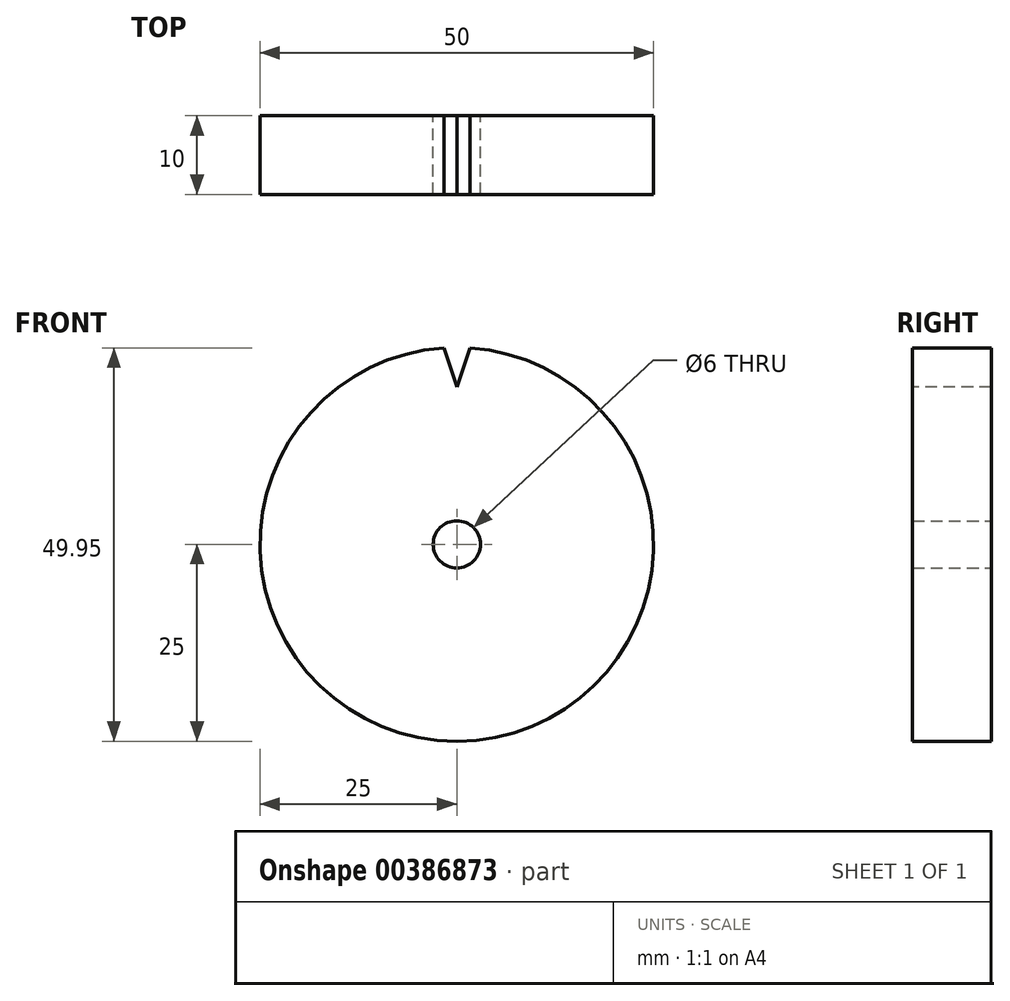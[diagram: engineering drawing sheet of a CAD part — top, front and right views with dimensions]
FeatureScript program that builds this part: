
annotation { "Feature Type Name" : "Feature", "Feature Type Description" : "" }
export const myFeature = defineFeature(function(context is Context, id is Id, definition is map)
    precondition{}
    {
        {
            var Q0;
            Q0=qCreatedBy(makeId("Front.planeOp"),FACE);
            var sketch = newSketch(context, id + "F0", { "sketchPlane" : qUnion([Q0])});
            skCircle(sketch, "E0", {"center": v(0, 0) * mm, "radius": 25 * mm});
            skCircle(sketch, "E1", {"center": v(0, 0) * mm, "radius": 3 * mm});
            skSolve(sketch);
        }
        {
            var Q0;
            Q0 = qSketchRegion(id + "F0", true);
            extrude(context, id + "F1", {"entities" : qUnion([Q0]), "depth" : 10 * mm});
        }
        {
            var Q0;
            Q0=makeQuery(id+"F1.opExtrude","CAP_FACE",FACE,{"disambiguationData":[OSD([sQuery(id+"F0.wireOp",EDGE,"E0"),sQuery(id+"F0.wireOp",EDGE,"E1")])],"isStart":false});
            var sketch = newSketch(context, id + "F2", { "sketchPlane" : qUnion([Q0])});
            skLineSegment(sketch, "E2", {"start": v(-2, 26) * mm, "end": v(0, 20) * mm});
            skLineSegment(sketch, "E3", {"start": v(0, 20) * mm, "end": v(2, 26) * mm});
            skLineSegment(sketch, "E4", {"start": v(2, 26) * mm, "end": v(-2, 26) * mm});
            skLineSegment(sketch, "E5", {"start": v(0, 20) * mm, "end": v(0, 24.85) * mm, "construction": true});
            skSolve(sketch);
        }
        {
            var Q0;
            Q0 = qSketchRegion(id + "F2", true);
            extrude(context, id + "F3", {"entities" : qUnion([Q0]), "operationType" : NewBodyOperationType.REMOVE, "oppositeDirection" : true, "depth" : 25 * mm});
        }
    });
